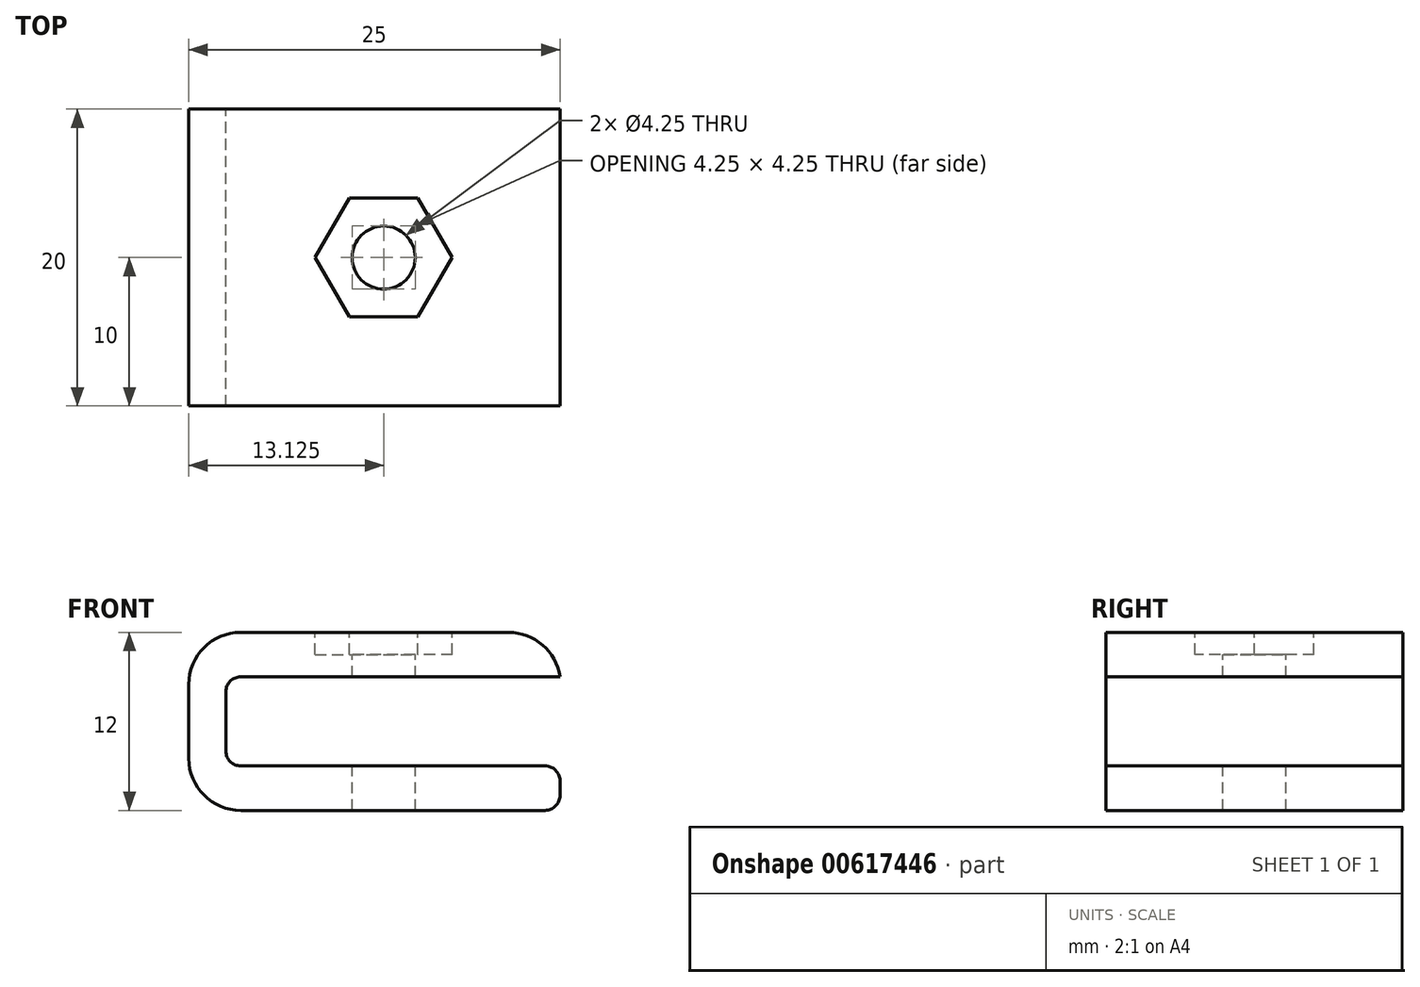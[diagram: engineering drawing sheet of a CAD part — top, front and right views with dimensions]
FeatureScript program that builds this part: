
annotation { "Feature Type Name" : "Feature", "Feature Type Description" : "" }
export const myFeature = defineFeature(function(context is Context, id is Id, definition is map)
    precondition{}
    {
        {
            var Q0;
            Q0=qCreatedBy(makeId("Front.planeOp"),FACE);
            var sketch = newSketch(context, id + "F0", { "sketchPlane" : qUnion([Q0])});
            skLineSegment(sketch, "E0.bottom", {"start": v(12.5, -16.5) * mm, "end": v(-12.5, -16.5) * mm, "construction": true});
            skLineSegment(sketch, "E0.top", {"start": v(12.5, 16.5) * mm, "end": v(-12.5, 16.5) * mm, "construction": true});
            skLineSegment(sketch, "E0.left", {"start": v(12.5, -16.5) * mm, "end": v(12.5, 16.5) * mm, "construction": true});
            skLineSegment(sketch, "E0.right", {"start": v(-12.5, -16.5) * mm, "end": v(-12.5, 16.5) * mm, "construction": true});
            skPoint(sketch, "E0.middle", {"position": v(0, 0) * mm});
            skLineSegment(sketch, "E1.bottom", {"start": v(-12.5, 16.5) * mm, "end": v(12.5, 16.5) * mm, "construction": true});
            skLineSegment(sketch, "E1.top", {"start": v(-12.5, 4.5) * mm, "end": v(12.5, 4.5) * mm, "construction": true});
            skLineSegment(sketch, "E1.left", {"start": v(-12.5, 16.5) * mm, "end": v(-12.5, 4.5) * mm, "construction": true});
            skLineSegment(sketch, "E1.right", {"start": v(12.5, 16.5) * mm, "end": v(12.5, 4.5) * mm, "construction": true});
            skLineSegment(sketch, "E2.bottom", {"start": v(-12.5, -16.5) * mm, "end": v(12.5, -16.5) * mm, "construction": true});
            skLineSegment(sketch, "E2.top", {"start": v(-12.5, -10.5) * mm, "end": v(12.5, -10.5) * mm, "construction": true});
            skLineSegment(sketch, "E2.left", {"start": v(-12.5, -16.5) * mm, "end": v(-12.5, -10.5) * mm, "construction": true});
            skLineSegment(sketch, "E2.right", {"start": v(12.5, -16.5) * mm, "end": v(12.5, -10.5) * mm, "construction": true});
            skLineSegment(sketch, "E3", {"start": v(12.5, 10.5) * mm, "end": v(-12.5, 10.5) * mm, "construction": true});
            skLineSegment(sketch, "E4", {"start": v(12.5, -13.5) * mm, "end": v(-12.5, -13.5) * mm, "construction": true});
            skLineSegment(sketch, "E5.bottom", {"start": v(-10, 13.5) * mm, "end": v(35, 13.5) * mm, "construction": true});
            skLineSegment(sketch, "E5.top", {"start": v(-10, 7.5) * mm, "end": v(35, 7.5) * mm, "construction": true});
            skLineSegment(sketch, "E5.left", {"start": v(-10, 13.5) * mm, "end": v(-10, 7.5) * mm, "construction": true});
            skLineSegment(sketch, "E5.right", {"start": v(35, 13.5) * mm, "end": v(35, 7.5) * mm, "construction": true});
            skPoint(sketch, "E5.middle", {"position": v(12.5, 10.5) * mm});
            skLineSegment(sketch, "E6.bottom", {"start": v(-10, -14.87) * mm, "end": v(35, -14.87) * mm, "construction": true});
            skLineSegment(sketch, "E6.top", {"start": v(-10, -12.12) * mm, "end": v(35, -12.12) * mm, "construction": true});
            skLineSegment(sketch, "E6.left", {"start": v(-10, -14.87) * mm, "end": v(-10, -12.12) * mm, "construction": true});
            skLineSegment(sketch, "E6.right", {"start": v(35, -14.87) * mm, "end": v(35, -12.12) * mm, "construction": true});
            skPoint(sketch, "E6.middle", {"position": v(12.5, -13.5) * mm});
            skLineSegment(sketch, "E7.bottom", {"start": v(-17.5, 9.25) * mm, "end": v(-7.5, 9.25) * mm, "construction": true});
            skLineSegment(sketch, "E7.top", {"start": v(-17.5, 11.75) * mm, "end": v(-7.5, 11.75) * mm, "construction": true});
            skLineSegment(sketch, "E7.left", {"start": v(-17.5, 9.25) * mm, "end": v(-17.5, 11.75) * mm, "construction": true});
            skLineSegment(sketch, "E7.right", {"start": v(-7.5, 9.25) * mm, "end": v(-7.5, 11.75) * mm, "construction": true});
            skPoint(sketch, "E7.middle", {"position": v(-12.5, 10.5) * mm});
            skLineSegment(sketch, "E8.bottom", {"start": v(-17.5, -12.25) * mm, "end": v(-7.5, -12.25) * mm, "construction": true});
            skLineSegment(sketch, "E8.top", {"start": v(-17.5, -14.75) * mm, "end": v(-7.5, -14.75) * mm, "construction": true});
            skLineSegment(sketch, "E8.left", {"start": v(-17.5, -12.25) * mm, "end": v(-17.5, -14.75) * mm, "construction": true});
            skLineSegment(sketch, "E8.right", {"start": v(-7.5, -12.25) * mm, "end": v(-7.5, -14.75) * mm, "construction": true});
            skPoint(sketch, "E8.middle", {"position": v(-12.5, -13.5) * mm});
            skLineSegment(sketch, "E9", {"start": v(0, 0) * mm, "end": v(-12.5, 0) * mm, "construction": true});
            skLineSegment(sketch, "E10", {"start": v(-17.5, 9.25) * mm, "end": v(-17.5, -12.25) * mm, "construction": true});
            skLineSegment(sketch, "E11", {"start": v(-17.5, 11.75) * mm, "end": v(-12.5, 11.75) * mm});
            skLineSegment(sketch, "E12", {"start": v(-12.5, 11.75) * mm, "end": v(-12.5, 16.5) * mm});
            skLineSegment(sketch, "E13", {"start": v(-12.5, 16.5) * mm, "end": v(12.5, 16.5) * mm});
            skLineSegment(sketch, "E14", {"start": v(12.5, 16.5) * mm, "end": v(12.5, 13.5) * mm});
            skLineSegment(sketch, "E15", {"start": v(12.5, 13.5) * mm, "end": v(-10, 13.5) * mm});
            skLineSegment(sketch, "E16", {"start": v(-10, 13.5) * mm, "end": v(-10, 7.5) * mm});
            skLineSegment(sketch, "E17", {"start": v(-10, 7.5) * mm, "end": v(12.5, 7.5) * mm});
            skLineSegment(sketch, "E18", {"start": v(12.5, 7.5) * mm, "end": v(12.5, 4.5) * mm});
            skLineSegment(sketch, "E19", {"start": v(12.5, 4.5) * mm, "end": v(-12.5, 4.5) * mm});
            skLineSegment(sketch, "E20", {"start": v(-12.5, 4.5) * mm, "end": v(-12.5, 9.25) * mm});
            skLineSegment(sketch, "E21", {"start": v(-12.5, 9.25) * mm, "end": v(-17.5, 9.25) * mm});
            skLineSegment(sketch, "E22", {"start": v(-17.5, -12.25) * mm, "end": v(-12.5, -12.25) * mm});
            skLineSegment(sketch, "E23", {"start": v(-12.5, -12.25) * mm, "end": v(-12.5, -10.5) * mm});
            skLineSegment(sketch, "E24", {"start": v(-12.5, -10.5) * mm, "end": v(12.5, -10.5) * mm});
            skLineSegment(sketch, "E25", {"start": v(12.5, -10.5) * mm, "end": v(12.5, -12.12) * mm});
            skLineSegment(sketch, "E26", {"start": v(12.5, -12.12) * mm, "end": v(-10, -12.12) * mm});
            skLineSegment(sketch, "E27", {"start": v(-10, -12.12) * mm, "end": v(-10, -14.87) * mm});
            skLineSegment(sketch, "E28", {"start": v(-10, -14.87) * mm, "end": v(12.5, -14.87) * mm});
            skLineSegment(sketch, "E29", {"start": v(12.5, -14.87) * mm, "end": v(12.5, -16.5) * mm});
            skLineSegment(sketch, "E30", {"start": v(12.5, -16.5) * mm, "end": v(-12.5, -16.5) * mm});
            skLineSegment(sketch, "E31", {"start": v(-12.5, -16.5) * mm, "end": v(-12.5, -14.75) * mm});
            skLineSegment(sketch, "E32", {"start": v(-12.5, -14.75) * mm, "end": v(-17.5, -14.75) * mm});
            skLineSegment(sketch, "E33", {"start": v(-10, 7.5) * mm, "end": v(-12.5, 7.5) * mm, "construction": true});
            skLineSegment(sketch, "E34", {"start": v(-12.5, 4.5) * mm, "end": v(-12.5, -10.5) * mm, "construction": true});
            skPoint(sketch, "E35", {"position": v(-12.5, -3) * mm});
            skLineSegment(sketch, "E36.bottom", {"start": v(-12.5, 7.5) * mm, "end": v(-17.5, 7.5) * mm});
            skLineSegment(sketch, "E36.top", {"start": v(-12.5, 4.5) * mm, "end": v(-17.5, 4.5) * mm});
            skLineSegment(sketch, "E36.left", {"start": v(-12.5, 7.5) * mm, "end": v(-12.5, 4.5) * mm});
            skLineSegment(sketch, "E36.right", {"start": v(-17.5, 7.5) * mm, "end": v(-17.5, 4.5) * mm});
            skLineSegment(sketch, "E37.bottom", {"start": v(-12.5, -10.5) * mm, "end": v(-17.5, -10.5) * mm});
            skLineSegment(sketch, "E37.top", {"start": v(-12.5, -12.25) * mm, "end": v(-17.5, -12.25) * mm});
            skLineSegment(sketch, "E37.left", {"start": v(-12.5, -10.5) * mm, "end": v(-12.5, -12.25) * mm});
            skLineSegment(sketch, "E37.right", {"start": v(-17.5, -10.5) * mm, "end": v(-17.5, -12.25) * mm});
            skLineSegment(sketch, "E38.bottom", {"start": v(-12.5, -13.5) * mm, "end": v(-17.5, -13.5) * mm});
            skLineSegment(sketch, "E38.left", {"start": v(-12.5, -13.5) * mm, "end": v(-12.5, -12.25) * mm});
            skLineSegment(sketch, "E38.right", {"start": v(-17.5, -13.5) * mm, "end": v(-17.5, -12.25) * mm});
            skPoint(sketch, "E39", {"position": v(-17.5, -3) * mm});
            skArc(sketch, "E40", {"start": v(-17.5, 4.5) * mm, "mid": v(-25, -3) * mm, "end": v(-17.5, -10.5) * mm});
            skArc(sketch, "E41", {"start": v(-17.5, 7.5) * mm, "mid": v(-28, -3) * mm, "end": v(-17.5, -13.5) * mm});
            skLineSegment(sketch, "E42", {"start": v(-12.5, 16.5) * mm, "end": v(-12.5, 7.5) * mm});
            skLineSegment(sketch, "E43", {"start": v(-12.5, -16.5) * mm, "end": v(-12.5, -13.5) * mm});
            skSolve(sketch);
        }
        {
            var Q0;
            {var subQ4=sQuery(id+"F0.wireOp",EDGE,"E13");Q0=makeQuery(id+"F0.imprint","IMPRINT",FACE,{"disambiguationData":[TD([[makeQuery(id+"F0.imprint","IMPRINT",EDGE,{"derivedFrom":subQ4}),-1.0]])]});}
            extrude(context, id + "F1", {"entities" : qUnion([Q0]), "depth" : 20 * mm, "offsetDistance" : 25 * mm});
        }
        {
            var Q0;
            Q0=makeQuery(id+"F1.opExtrude","SWEPT_FACE",FACE,{"disambiguationData":[OSD([sQuery(id+"F0.wireOp",EDGE,"E13")])]});
            var sketch = newSketch(context, id + "F2", { "sketchPlane" : qUnion([Q0])});
            skLineSegment(sketch, "E44.bottom", {"start": v(-10, 0) * mm, "end": v(12.5, 0) * mm, "construction": true});
            skLineSegment(sketch, "E44.top", {"start": v(-10, -20) * mm, "end": v(12.5, -20) * mm, "construction": true});
            skLineSegment(sketch, "E44.left", {"start": v(-10, 0) * mm, "end": v(-10, -20) * mm, "construction": true});
            skLineSegment(sketch, "E44.right", {"start": v(12.5, 0) * mm, "end": v(12.5, -20) * mm, "construction": true});
            skLineSegment(sketch, "E45", {"start": v(0, 0) * mm, "end": v(1.25, -20) * mm, "construction": true});
            skCircle(sketch, "E46", {"center": v(0.63, -10) * mm, "radius": 2.12 * mm});
            skSolve(sketch);
        }
        {
            var Q0;
            Q0=makeQuery(id+"F2.imprint","IMPRINT",FACE,{"disambiguationData":[TD([[makeQuery(id+"F2.imprint","IMPRINT",EDGE,{"derivedFrom":sQuery(id+"F2.wireOp",EDGE,"E46")}),1.0]])]});
            var Q1;
            Q1=makeQuery(id+"F1.opExtrude","SWEPT_FACE",FACE,{"disambiguationData":[OSD([sQuery(id+"F0.wireOp",EDGE,"E19")])]});
            extrude(context, id + "F3", {"entities" : qUnion([Q0]), "operationType" : NewBodyOperationType.REMOVE, "endBound" : BoundingType.UP_TO_SURFACE, "oppositeDirection" : true, "depth" : 25 * mm, "endBoundEntityFace" : qUnion([Q1]), "offsetDistance" : 25 * mm});
        }
        {
            var Q0;
            Q0=makeQuery(id+"F1.opExtrude","SWEPT_FACE",FACE,{"disambiguationData":[OSD([sQuery(id+"F0.wireOp",EDGE,"E13")])]});
            var sketch = newSketch(context, id + "F4", { "sketchPlane" : qUnion([Q0])});
            skCircle(sketch, "E47.cCircle", {"center": v(0.63, -10) * mm, "radius": 4 * mm, "construction": true});
            skLineSegment(sketch, "E47.0", {"start": v(5.24, -10) * mm, "end": v(2.93, -14) * mm});
            skLineSegment(sketch, "E47.1", {"start": v(2.93, -14) * mm, "end": v(-1.68, -14) * mm});
            skLineSegment(sketch, "E47.2", {"start": v(-1.68, -14) * mm, "end": v(-4, -10) * mm});
            skLineSegment(sketch, "E47.3", {"start": v(-4, -10) * mm, "end": v(-1.68, -6) * mm});
            skLineSegment(sketch, "E47.4", {"start": v(-1.68, -6) * mm, "end": v(2.93, -6) * mm});
            skLineSegment(sketch, "E47.5", {"start": v(2.93, -6) * mm, "end": v(5.24, -10) * mm});
            skPoint(sketch, "E47.0.midPoint", {"position": v(4.09, -12) * mm});
            skSolve(sketch);
        }
        {
            var Q0;
            Q0=makeQuery(id+"F4.imprint","IMPRINT",FACE,{"disambiguationData":[TD([[makeQuery(id+"F4.imprint","IMPRINT",EDGE,{"derivedFrom":sQuery(id+"F4.wireOp",EDGE,"E47.0")}),-1.0]])]});
            extrude(context, id + "F5", {"entities" : qUnion([Q0]), "operationType" : NewBodyOperationType.REMOVE, "oppositeDirection" : true, "depth" : 1.5 * mm, "offsetDistance" : 25 * mm});
        }
        {
            var Q0;
            Q0=makeQuery(id+"F1.opExtrude","SWEPT_EDGE",EDGE,{"disambiguationData":[OSD([sQuery(id+"F0.wireOp",EDGE,"E36.bottom"),sQuery(id+"F0.wireOp",EDGE,"E36.left"),sQuery(id+"F0.wireOp",EDGE,"E42")])]});
            var Q1;
            Q1=makeQuery(id+"F1.opExtrude","SWEPT_EDGE",EDGE,{"disambiguationData":[OSD([sQuery(id+"F0.wireOp",EDGE,"E13"),sQuery(id+"F0.wireOp",EDGE,"E42")])]});
            var Q2;
            Q2=makeQuery(id+"F1.opExtrude","SWEPT_EDGE",EDGE,{"disambiguationData":[OSD([sQuery(id+"F0.wireOp",EDGE,"E19"),sQuery(id+"F0.wireOp",EDGE,"E36.top"),sQuery(id+"F0.wireOp",EDGE,"E36.left")])]});
            fillet(context, id + "F6", {"entities" : qUnion([Q0, Q1, Q2]), "radius" : 3.5 * mm, "tangentPropagation" : true, "allowEdgeOverflow" : false});
        }
        {
            var Q0;
            Q0=makeQuery(id+"F1.opExtrude","SWEPT_EDGE",EDGE,{"disambiguationData":[OSD([sQuery(id+"F0.wireOp",EDGE,"E15"),sQuery(id+"F0.wireOp",EDGE,"E16")])]});
            var Q1;
            Q1=makeQuery(id+"F1.opExtrude","SWEPT_EDGE",EDGE,{"disambiguationData":[OSD([sQuery(id+"F0.wireOp",EDGE,"E16"),sQuery(id+"F0.wireOp",EDGE,"E17")])]});
            var Q2;
            Q2=makeQuery(id+"F1.opExtrude","SWEPT_EDGE",EDGE,{"disambiguationData":[OSD([sQuery(id+"F0.wireOp",EDGE,"E17"),sQuery(id+"F0.wireOp",EDGE,"E18")])]});
            var Q3;
            Q3=makeQuery(id+"F1.opExtrude","SWEPT_EDGE",EDGE,{"disambiguationData":[OSD([sQuery(id+"F0.wireOp",EDGE,"E14"),sQuery(id+"F0.wireOp",EDGE,"E15")])]});
            var Q4;
            Q4=makeQuery(id+"F6.opFillet","BLEND_EDGE",EDGE,{"blendedFrom":[makeQuery(id+"F1.opExtrude","SWEPT_EDGE",EDGE,{"disambiguationData":[OSD([sQuery(id+"F0.wireOp",EDGE,"E20"),sQuery(id+"F0.wireOp",EDGE,"E21")])]}),makeQuery(id+"F1.opExtrude","SWEPT_FACE",FACE,{"disambiguationData":[OSD([sQuery(id+"F0.wireOp",EDGE,"E19")])]})],"blendedInto":[makeQuery(id+"F1.opExtrude","SWEPT_FACE",FACE,{"disambiguationData":[OSD([sQuery(id+"F0.wireOp",EDGE,"E19")])]})]});
            var Q5;
            Q5=makeQuery(id+"F6.opFillet","BLEND_EDGE",EDGE,{"blendedFrom":[makeQuery(id+"F1.opExtrude","SWEPT_EDGE",EDGE,{"disambiguationData":[OSD([sQuery(id+"F0.wireOp",EDGE,"E11"),sQuery(id+"F0.wireOp",EDGE,"E12")])]}),makeQuery(id+"F1.opExtrude","SWEPT_FACE",FACE,{"disambiguationData":[OSD([sQuery(id+"F0.wireOp",EDGE,"E13")])]})],"blendedInto":[makeQuery(id+"F1.opExtrude","SWEPT_FACE",FACE,{"disambiguationData":[OSD([sQuery(id+"F0.wireOp",EDGE,"E13")])]})]});
            var Q6;
            Q6=makeQuery(id+"F1.opExtrude","SWEPT_EDGE",EDGE,{"disambiguationData":[OSD([sQuery(id+"F0.wireOp",EDGE,"E18"),sQuery(id+"F0.wireOp",EDGE,"E19")])]});
            var Q7;
            Q7=makeQuery(id+"F1.opExtrude","SWEPT_EDGE",EDGE,{"disambiguationData":[OSD([sQuery(id+"F0.wireOp",EDGE,"E13"),sQuery(id+"F0.wireOp",EDGE,"E14")])]});
            fillet(context, id + "F7", {"entities" : qUnion([Q0, Q1, Q2, Q3, Q4, Q5, Q6, Q7]), "radius" : 1 * mm, "tangentPropagation" : true, "allowEdgeOverflow" : false});
        }
    });
